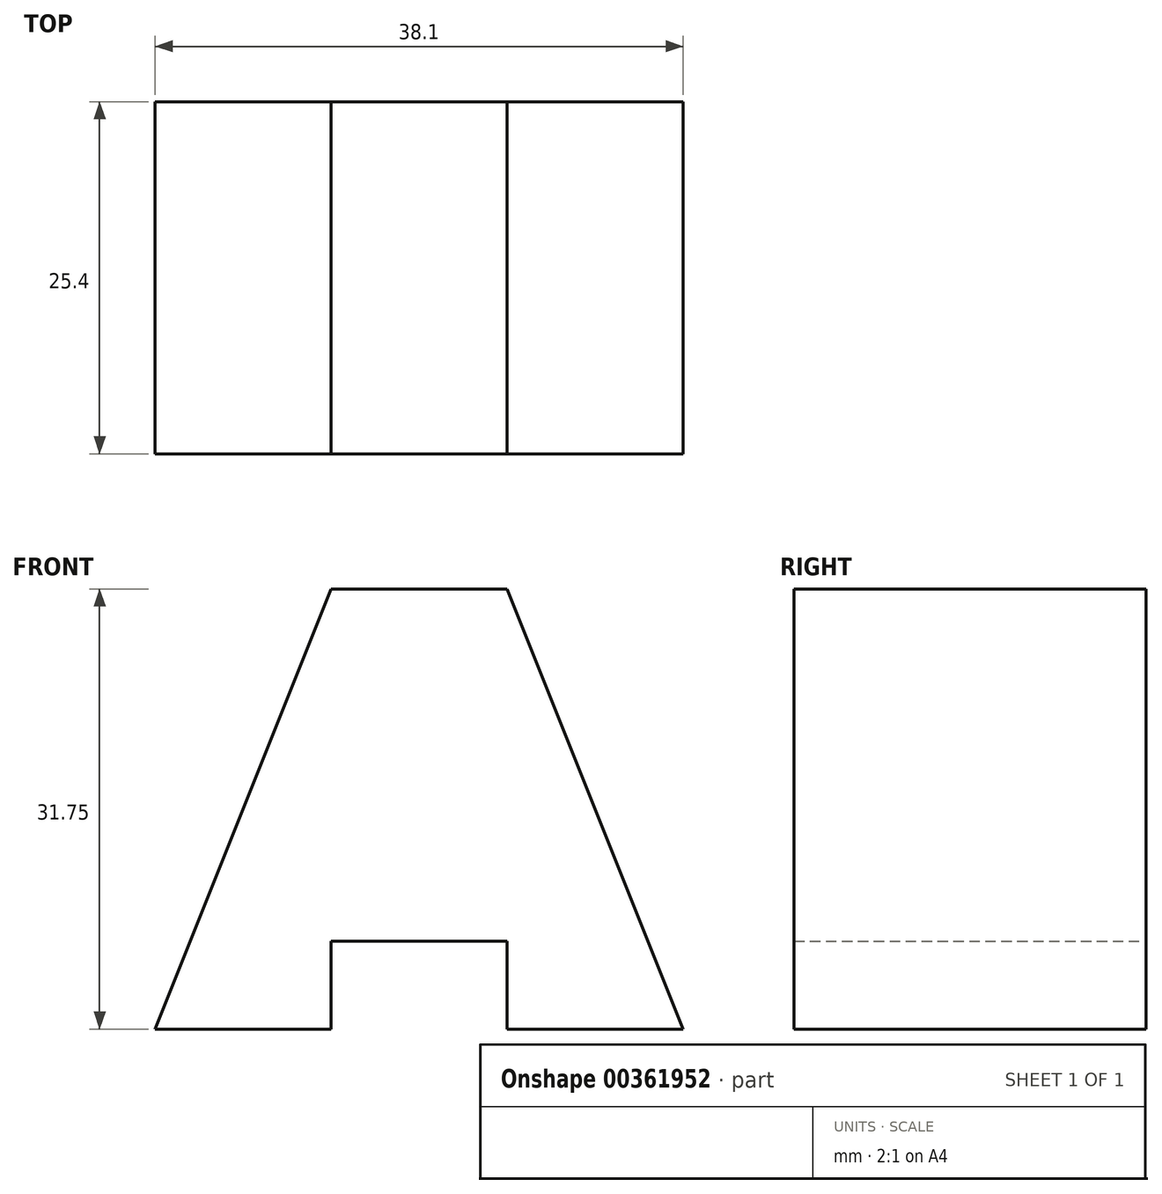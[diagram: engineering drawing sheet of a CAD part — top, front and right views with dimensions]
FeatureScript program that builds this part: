
annotation { "Feature Type Name" : "Feature", "Feature Type Description" : "" }
export const myFeature = defineFeature(function(context is Context, id is Id, definition is map)
    precondition{}
    {
        {
            var Q0;
            Q0=qCreatedBy(makeId("Front.planeOp"),FACE);
            var sketch = newSketch(context, id + "F0", { "sketchPlane" : qUnion([Q0])});
            skLineSegment(sketch, "E0", {"start": v(0, 0) * mm, "end": v(0, 31.75) * mm});
            skLineSegment(sketch, "E1", {"start": v(0, 31.75) * mm, "end": v(38.1, 31.75) * mm});
            skLineSegment(sketch, "E2", {"start": v(38.1, 31.75) * mm, "end": v(38.1, 0) * mm});
            skLineSegment(sketch, "E3", {"start": v(38.1, 0) * mm, "end": v(0, 0) * mm});
            skSolve(sketch);
        }
        {
            var Q0;
            Q0 = qSketchRegion(id + "F0", true);
            extrude(context, id + "F1", {"entities" : qUnion([Q0]), "depth" : 25.4 * mm});
        }
        {
            var Q0;
            Q0=makeQuery(id+"F1.opExtrude","CAP_FACE",FACE,{"disambiguationData":[OSD([sQuery(id+"F0.wireOp",EDGE,"E0"),sQuery(id+"F0.wireOp",EDGE,"E1"),sQuery(id+"F0.wireOp",EDGE,"E2"),sQuery(id+"F0.wireOp",EDGE,"E3")])],"isStart":false});
            var sketch = newSketch(context, id + "F2", { "sketchPlane" : qUnion([Q0])});
            skLineSegment(sketch, "E4", {"start": v(12.7, 31.75) * mm, "end": v(0, 0) * mm});
            skLineSegment(sketch, "E5", {"start": v(25.4, 31.75) * mm, "end": v(38.1, 0) * mm});
            skSolve(sketch);
        }
        {
            var Q0;
            {var subQ0=sQuery(id+"F2.wireOp",EDGE,"E5");Q0=makeQuery(id+"F2.imprint","IMPRINT",FACE,{"disambiguationData":[TD([[makeQuery(id+"F2.imprint","IMPRINT",EDGE,{"derivedFrom":subQ0}),1.0]])]});}
            var Q1;
            {var subQ0=sQuery(id+"F2.wireOp",EDGE,"E4");Q1=makeQuery(id+"F2.imprint","IMPRINT",FACE,{"disambiguationData":[TD([[makeQuery(id+"F2.imprint","IMPRINT",EDGE,{"derivedFrom":subQ0}),-1.0]])]});}
            extrude(context, id + "F3", {"entities" : qUnion([Q0, Q1]), "operationType" : NewBodyOperationType.REMOVE, "oppositeDirection" : true, "depth" : 25.4 * mm});
        }
        {
            var Q0;
            Q0=makeQuery(id+"F1.opExtrude","SWEPT_FACE",FACE,{"disambiguationData":[OSD([sQuery(id+"F0.wireOp",EDGE,"E3")])]});
            var sketch = newSketch(context, id + "F4", { "sketchPlane" : qUnion([Q0])});
            skLineSegment(sketch, "E6", {"start": v(12.7, 25.4) * mm, "end": v(12.7, 0) * mm});
            skLineSegment(sketch, "E7", {"start": v(12.7, 0) * mm, "end": v(25.4, 0) * mm});
            skLineSegment(sketch, "E8", {"start": v(25.4, 0) * mm, "end": v(25.4, 25.4) * mm});
            skLineSegment(sketch, "E9", {"start": v(25.4, 25.4) * mm, "end": v(12.7, 25.4) * mm});
            skSolve(sketch);
        }
        {
            var Q0;
            Q0 = qSketchRegion(id + "F4", true);
            extrude(context, id + "F5", {"entities" : qUnion([Q0]), "operationType" : NewBodyOperationType.REMOVE, "oppositeDirection" : true, "depth" : 6.35 * mm});
        }
    });
